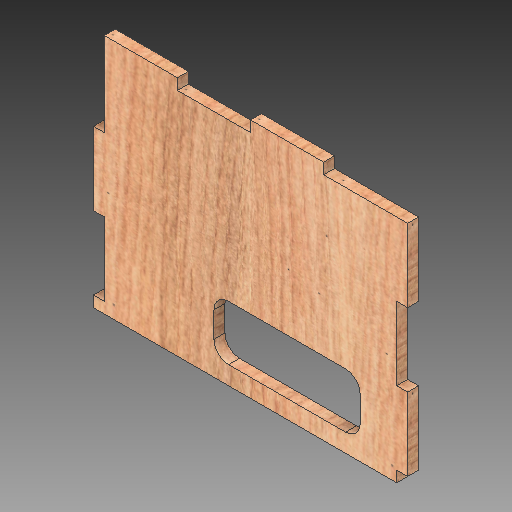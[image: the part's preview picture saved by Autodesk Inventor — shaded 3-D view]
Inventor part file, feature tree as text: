
AUTODESK INVENTOR PART (.ipt)
format: ipt  version: 2018.2 (Build 222227000, 227)  size: 354,304 bytes
history: native  units: mm
features: extrude x2, sketch x2, fillet x1
ambient origin geometry x8: Origin, YZ Plane, XZ Plane, XY Plane, X Axis, Y Axis, Z Axis, Center Point
bodies: Solid1 (feature_tree)
feature tree (5):
  extrude  "Extrusion1"  Depth=3.0mm
  extrude  "Extrusion2"  Depth=20.0mm
  fillet  "Fillet1"  Radius=20.0mm
  sketch  "Sketch1"  dims[d0=83.0mm d1=3.0mm]
  sketch  "Sketch2"  dims[d2=3.0mm d3=20.0mm d4=20.0mm d5=20.0mm d6=3.0mm d7=20.0mm d8=20.0mm d9=20.0mm d10=20.0mm d11=3.0mm d12=20.0mm d13=3.0mm d14=20.0mm d16=20.0mm d17=3.0mm d18=0.0mm d19=5.0mm d20=10.0mm d21=15.0mm d22=40.0mm d23=10.0mm d24=0.0mm d25=4.0mm]
